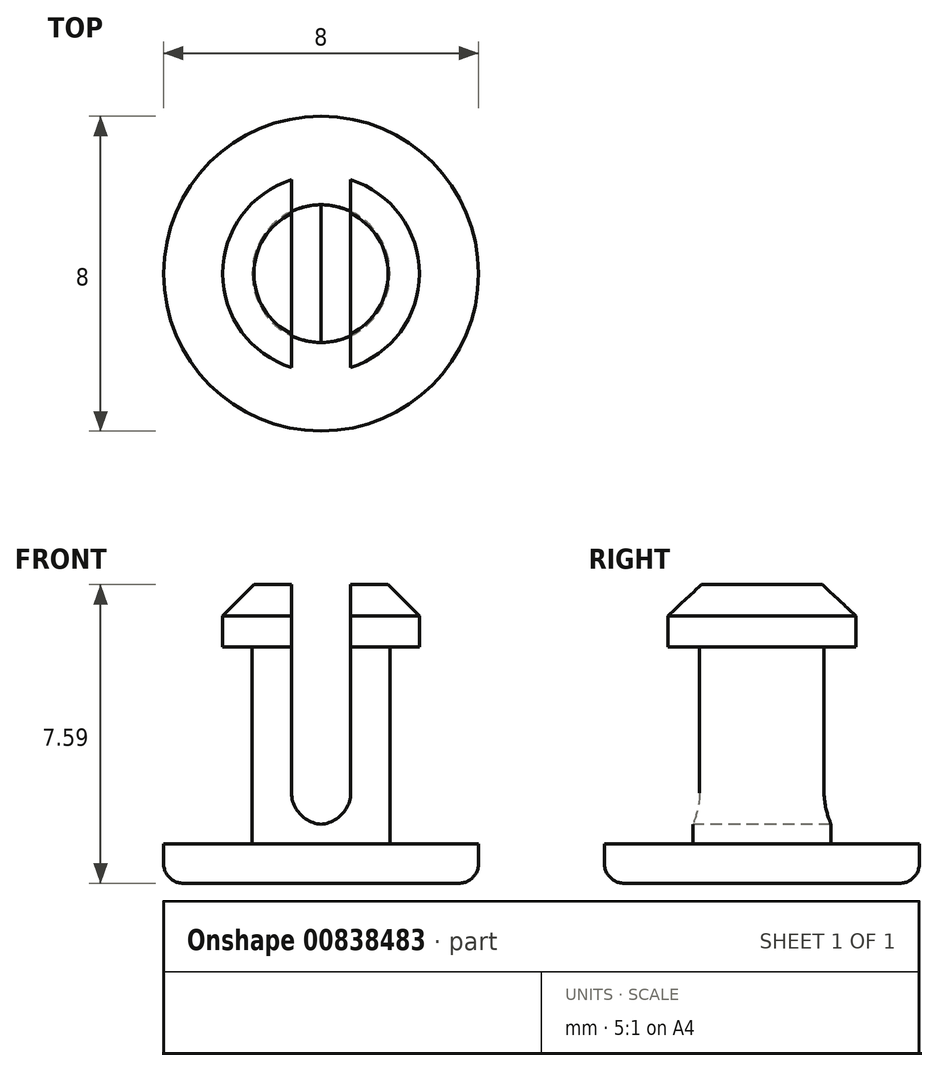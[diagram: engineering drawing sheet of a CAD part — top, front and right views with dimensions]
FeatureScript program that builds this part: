
annotation { "Feature Type Name" : "Feature", "Feature Type Description" : "" }
export const myFeature = defineFeature(function(context is Context, id is Id, definition is map)
    precondition{}
    {
        {
            var Q0;
            Q0=qCreatedBy(makeId("Front.planeOp"),FACE);
            var sketch = newSketch(context, id + "F0", { "sketchPlane" : qUnion([Q0])});
            skLineSegment(sketch, "E0.bottom", {"start": v(1.75, 0) * mm, "end": v(4, 0) * mm});
            skLineSegment(sketch, "E0.top", {"start": v(0, -1) * mm, "end": v(4, -1) * mm});
            skLineSegment(sketch, "E0.left", {"start": v(0, 0) * mm, "end": v(0, -1) * mm});
            skLineSegment(sketch, "E0.right", {"start": v(4, 0) * mm, "end": v(4, -1) * mm});
            skLineSegment(sketch, "E1.left", {"start": v(0, 0) * mm, "end": v(0, 5) * mm});
            skLineSegment(sketch, "E1.right", {"start": v(1.75, 0) * mm, "end": v(1.75, 5) * mm});
            skLineSegment(sketch, "E2.bottom", {"start": v(1.75, 5) * mm, "end": v(2.5, 5) * mm});
            skLineSegment(sketch, "E2.top", {"start": v(0, 6.59) * mm, "end": v(2.5, 6.59) * mm});
            skLineSegment(sketch, "E2.left", {"start": v(0, 5) * mm, "end": v(0, 6.59) * mm});
            skLineSegment(sketch, "E2.right", {"start": v(2.5, 5) * mm, "end": v(2.5, 6.59) * mm});
            skSolve(sketch);
        }
        {
            var Q0;
            Q0=qSketchRegion(id+"F0",true);
            var Q1;
            Q1=sQuery(id+"F0.wireOp",EDGE,"E1.left");
            revolve(context, id + "F1", {"entities" : qUnion([Q0]), "axis" : qUnion([Q1]), "revolveType" : RevolveType.FULL});
        }
        {
            var Q0;
            Q0=makeQuery(id+"F1.opRevolve","SWEPT_EDGE",EDGE,{"disambiguationData":[OSD([sQuery(id+"F0.wireOp",EDGE,"E2.top"),sQuery(id+"F0.wireOp",EDGE,"E2.right")])]});
            chamfer(context, id + "F2", {"entities" : qUnion([Q0]), "width" : 0.8 * mm, "tangentPropagation" : true});
        }
        {
            var Q0;
            Q0=qCreatedBy(makeId("Front.planeOp"),FACE);
            var sketch = newSketch(context, id + "F3", { "sketchPlane" : qUnion([Q0])});
            skLineSegment(sketch, "E3.left", {"start": v(-0.75, 0.5) * mm, "end": v(-0.75, 6.59) * mm});
            skLineSegment(sketch, "E3.right", {"start": v(0.75, 0.5) * mm, "end": v(0.75, 6.59) * mm});
            skLineSegment(sketch, "E4.0", {"start": v(-0.75, 6.59) * mm, "end": v(0.75, 6.59) * mm});
            skLineSegment(sketch, "E5", {"start": v(-0.75, 0.5) * mm, "end": v(0.75, 0.5) * mm});
            skLineSegment(sketch, "E6", {"start": v(0, 0) * mm, "end": v(0, 0.5) * mm, "construction": true});
            skSolve(sketch);
        }
        {
            var Q0;
            Q0=qSketchRegion(id+"F3",true);
            extrude(context, id + "F4", {"entities" : qUnion([Q0]), "operationType" : NewBodyOperationType.REMOVE, "endBound" : BoundingType.THROUGH_ALL, "depth" : 25.4 * mm, "offsetDistance" : 25.4 * mm, "hasSecondDirection" : true, "secondDirectionBound" : SecondDirectionBoundingType.THROUGH_ALL, "secondDirectionOppositeDirection" : true, "secondDirectionDepth" : 25.4 * mm});
        }
        {
            var Q0;
            Q0=makeQuery(id+"F4.boolean.opBoolean","COPY",EDGE,{"derivedFrom":makeQuery(id+"F4.opExtrude","SWEPT_EDGE",EDGE,{"disambiguationData":[OSD([sQuery(id+"F3.wireOp",EDGE,"E3.right"),sQuery(id+"F3.wireOp",EDGE,"E5")])]})});
            var Q1;
            Q1=makeQuery(id+"F4.boolean.opBoolean","COPY",EDGE,{"derivedFrom":makeQuery(id+"F4.opExtrude","SWEPT_EDGE",EDGE,{"disambiguationData":[OSD([sQuery(id+"F3.wireOp",EDGE,"E3.left"),sQuery(id+"F3.wireOp",EDGE,"E5")])]})});
            fillet(context, id + "F5", {"entities" : qUnion([Q0, Q1]), "radius" : 0.8 * mm, "tangentPropagation" : true, "allowEdgeOverflow" : false});
        }
        {
            var Q0;
            Q0=makeQuery(id+"F1.opRevolve","SWEPT_EDGE",EDGE,{"disambiguationData":[OSD([sQuery(id+"F0.wireOp",EDGE,"E0.top"),sQuery(id+"F0.wireOp",EDGE,"E0.right")])]});
            fillet(context, id + "F6", {"entities" : qUnion([Q0]), "radius" : .5 * mm, "tangentPropagation" : true, "allowEdgeOverflow" : false});
        }
    });
